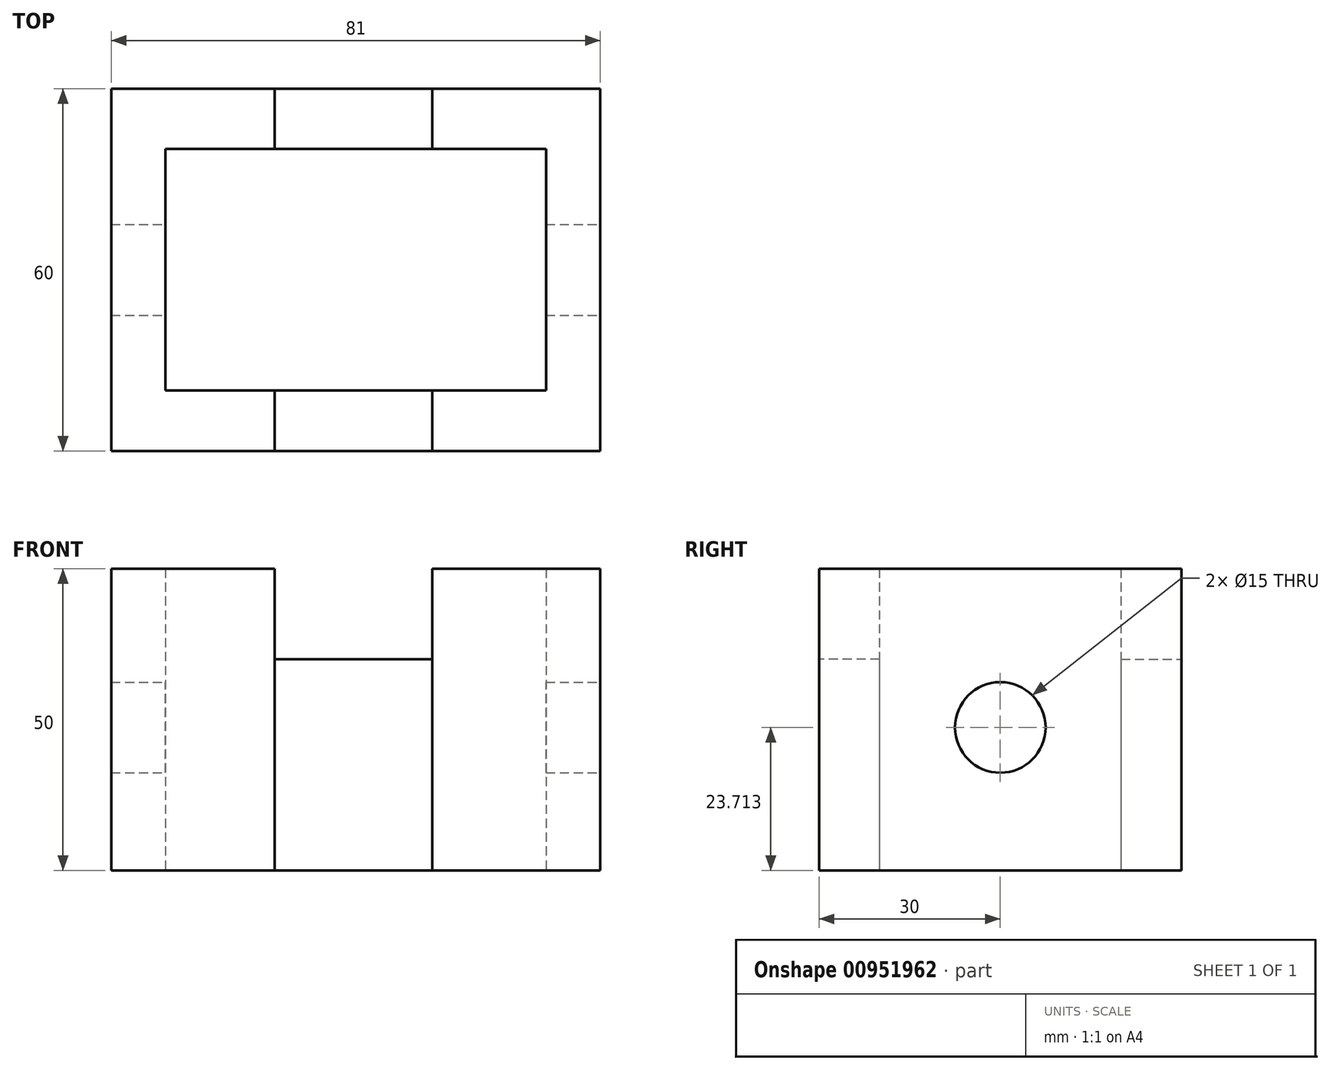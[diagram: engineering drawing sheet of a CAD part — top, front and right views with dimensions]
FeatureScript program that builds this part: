
annotation { "Feature Type Name" : "Feature", "Feature Type Description" : "" }
export const myFeature = defineFeature(function(context is Context, id is Id, definition is map)
    precondition{}
    {
        {
            var Q0;
            Q0=qCreatedBy(makeId("Top.planeOp"),FACE);
            var sketch = newSketch(context, id + "F0", { "sketchPlane" : qUnion([Q0])});
            skLineSegment(sketch, "E0.bottom", {"start": v(-39.65, 30) * mm, "end": v(41.35, 30) * mm});
            skLineSegment(sketch, "E0.top", {"start": v(-39.65, -30) * mm, "end": v(41.35, -30) * mm});
            skLineSegment(sketch, "E0.left", {"start": v(-39.65, 30) * mm, "end": v(-39.65, -30) * mm});
            skLineSegment(sketch, "E0.right", {"start": v(41.35, 30) * mm, "end": v(41.35, -30) * mm});
            skLineSegment(sketch, "E1.bottom", {"start": v(-30.65, 20) * mm, "end": v(32.35, 20) * mm});
            skLineSegment(sketch, "E1.top", {"start": v(-30.65, -20) * mm, "end": v(32.35, -20) * mm});
            skLineSegment(sketch, "E1.left", {"start": v(-30.65, 20) * mm, "end": v(-30.65, -20) * mm});
            skLineSegment(sketch, "E1.right", {"start": v(32.35, 20) * mm, "end": v(32.35, -20) * mm});
            skLineSegment(sketch, "E2", {"start": v(-12.57, 20) * mm, "end": v(-12.57, 30) * mm});
            skLineSegment(sketch, "E3", {"start": v(13.55, 20) * mm, "end": v(13.55, 30) * mm});
            skLineSegment(sketch, "E4", {"start": v(-12.57, -20) * mm, "end": v(-12.57, -30) * mm});
            skLineSegment(sketch, "E5", {"start": v(13.55, -20) * mm, "end": v(13.55, -30) * mm});
            skSolve(sketch);
        }
        {
            var Q0;
            {var subQ0=sQuery(id+"F0.wireOp",EDGE,"E0.left");Q0=makeQuery(id+"F0.imprint","IMPRINT",FACE,{"disambiguationData":[TD([[makeQuery(id+"F0.imprint","IMPRINT",EDGE,{"derivedFrom":subQ0}),1.0]])]});}
            var Q1;
            {var subQ3=sQuery(id+"F0.wireOp",EDGE,"E0.right");Q1=makeQuery(id+"F0.imprint","IMPRINT",FACE,{"disambiguationData":[TD([[makeQuery(id+"F0.imprint","IMPRINT",EDGE,{"derivedFrom":subQ3}),-1.0]])]});}
            extrude(context, id + "F1", {"entities" : qUnion([Q0, Q1]), "depth" : 50 * mm, "offsetDistance" : 25 * mm});
        }
        {
            var Q0;
            {var subQ0=sQuery(id+"F0.wireOp",EDGE,"E4");Q0=makeQuery(id+"F0.imprint","IMPRINT",FACE,{"disambiguationData":[TD([[makeQuery(id+"F0.imprint","IMPRINT",EDGE,{"derivedFrom":subQ0}),1.0]])]});}
            var Q1;
            {var subQ0=sQuery(id+"F0.wireOp",EDGE,"E2");Q1=makeQuery(id+"F0.imprint","IMPRINT",FACE,{"disambiguationData":[TD([[makeQuery(id+"F0.imprint","IMPRINT",EDGE,{"derivedFrom":subQ0}),-1.0]])]});}
            extrude(context, id + "F2", {"entities" : qUnion([Q0, Q1]), "depth" : 35 * mm, "offsetDistance" : 25 * mm});
        }
        {
            var Q0;
            Q0=makeQuery(id+"F1.opExtrude","SWEPT_FACE",FACE,{"disambiguationData":[OSD([sQuery(id+"F0.wireOp",EDGE,"E0.right")])]});
            var sketch = newSketch(context, id + "F3", { "sketchPlane" : qUnion([Q0])});
            skCircle(sketch, "E6", {"center": v(0, 23.71) * mm, "radius": 7.5 * mm});
            skSolve(sketch);
        }
        {
            var Q0;
            Q0=sQuery(id+"F3.wireOp",VERTEX,"E6.center");
            var Q1;
            Q1=makeQuery(id+"F1.opExtrude","SWEPT_BODY",BODY,{"disambiguationData":[OSD([sQuery(id+"F0.wireOp",EDGE,"E0.bottom"),sQuery(id+"F0.wireOp",EDGE,"E0.top"),sQuery(id+"F0.wireOp",EDGE,"E0.left"),sQuery(id+"F0.wireOp",EDGE,"E1.bottom"),sQuery(id+"F0.wireOp",EDGE,"E1.top"),sQuery(id+"F0.wireOp",EDGE,"E1.left"),sQuery(id+"F0.wireOp",EDGE,"E2"),sQuery(id+"F0.wireOp",EDGE,"E4")])]});
            var Q2;
            Q2=makeQuery(id+"F1.opExtrude","SWEPT_BODY",BODY,{"disambiguationData":[OSD([sQuery(id+"F0.wireOp",EDGE,"E0.bottom"),sQuery(id+"F0.wireOp",EDGE,"E0.top"),sQuery(id+"F0.wireOp",EDGE,"E0.right"),sQuery(id+"F0.wireOp",EDGE,"E1.bottom"),sQuery(id+"F0.wireOp",EDGE,"E1.top"),sQuery(id+"F0.wireOp",EDGE,"E1.right"),sQuery(id+"F0.wireOp",EDGE,"E3"),sQuery(id+"F0.wireOp",EDGE,"E5")])]});
            hole(context, id + "F4", {"style" : HoleStyle.SIMPLE, "endStyle" : HoleEndStyle.THROUGH, "holeDiameter" : 15 * mm, "majorDiameter" : 5 * mm, "isTappedThrough" : true, "tappedDepth" : 12 * mm, "tapClearance" : 3, "locations" : qUnion([Q0]), "scope" : qUnion([Q1, Q2])});
        }
    });
